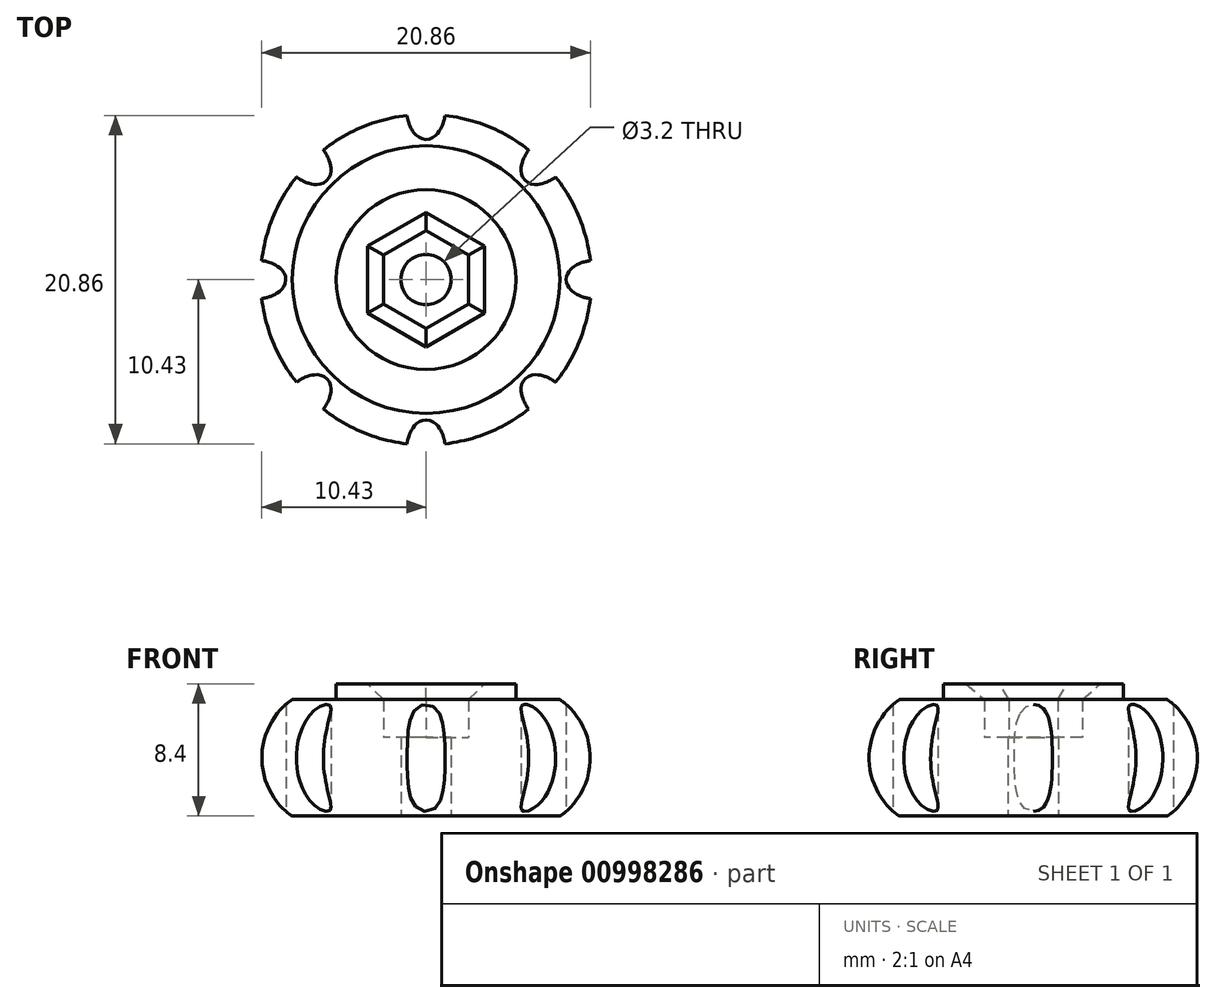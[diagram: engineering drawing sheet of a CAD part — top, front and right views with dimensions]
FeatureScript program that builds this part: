
annotation { "Feature Type Name" : "Feature", "Feature Type Description" : "" }
export const myFeature = defineFeature(function(context is Context, id is Id, definition is map)
    precondition{}
    {
        {
            var Q0;
            Q0=qCreatedBy(makeId("Top.planeOp"),FACE);
            var sketch = newSketch(context, id + "F0", { "sketchPlane" : qUnion([Q0])});
            skCircle(sketch, "E0", {"center": v(0, 0) * mm, "radius": 1.6 * mm});
            skCircle(sketch, "E1", {"center": v(0, 0) * mm, "radius": 8.5 * mm});
            skCircle(sketch, "E2.cCircle", {"center": v(0, 0) * mm, "radius": 2.7 * mm, "construction": true});
            skLineSegment(sketch, "E2.0", {"start": v(-2.7, 1.56) * mm, "end": v(0, 3.12) * mm});
            skLineSegment(sketch, "E2.1", {"start": v(0, 3.12) * mm, "end": v(2.7, 1.56) * mm});
            skLineSegment(sketch, "E2.2", {"start": v(2.7, 1.56) * mm, "end": v(2.7, -1.56) * mm});
            skLineSegment(sketch, "E2.3", {"start": v(2.7, -1.56) * mm, "end": v(0, -3.12) * mm});
            skLineSegment(sketch, "E2.4", {"start": v(0, -3.12) * mm, "end": v(-2.7, -1.56) * mm});
            skLineSegment(sketch, "E2.5", {"start": v(-2.7, -1.56) * mm, "end": v(-2.7, 1.56) * mm});
            skPoint(sketch, "E2.0.midPoint", {"position": v(-1.35, 2.34) * mm});
            skLineSegment(sketch, "E3", {"start": v(-8.5, 0) * mm, "end": v(8.5, 0) * mm, "construction": true});
            skSolve(sketch);
        }
        {
            var Q0;
            Q0=makeQuery(id+"F0.imprint","IMPRINT",FACE,{"disambiguationData":[TD([[makeQuery(id+"F0.imprint","IMPRINT",EDGE,{"derivedFrom":sQuery(id+"F0.wireOp",EDGE,"E1")}),1.0]])]});
            var Q1;
            Q1=makeQuery(id+"F0.imprint","IMPRINT",FACE,{"disambiguationData":[TD([[makeQuery(id+"F0.imprint","IMPRINT",EDGE,{"derivedFrom":sQuery(id+"F0.wireOp",EDGE,"E0")}),-1.0]])]});
            extrude(context, id + "F1", {"entities" : qUnion([Q0, Q1]), "depth" : 5 * mm, "offsetDistance" : 25 * mm});
        }
        {
            var Q0;
            Q0=makeQuery(id+"F0.imprint","IMPRINT",FACE,{"disambiguationData":[TD([[makeQuery(id+"F0.imprint","IMPRINT",EDGE,{"derivedFrom":sQuery(id+"F0.wireOp",EDGE,"E1")}),1.0]])]});
            extrude(context, id + "F2", {"entities" : qUnion([Q0]), "operationType" : NewBodyOperationType.ADD, "depth" : 7.4 * mm, "offsetDistance" : 25 * mm});
        }
        {
            var Q0;
            Q0=qCreatedBy(makeId("Front.planeOp"),FACE);
            var sketch = newSketch(context, id + "F3", { "sketchPlane" : qUnion([Q0])});
            skArc(sketch, "E4", {"start": v(8.5, 0) * mm, "mid": v(10.5, 3.7) * mm, "end": v(8.5, 7.4) * mm});
            skLineSegment(sketch, "E5", {"start": v(8.5, 7.4) * mm, "end": v(8.5, 0) * mm});
            skSolve(sketch);
        }
        {
            var Q0;
            Q0=makeQuery(id+"F3.imprint","IMPRINT",FACE,{"disambiguationData":[TD([[makeQuery(id+"F3.imprint","IMPRINT",EDGE,{"derivedFrom":sQuery(id+"F3.wireOp",EDGE,"E4")}),1.0]])]});
            var Q1;
            {var subQ0=sQuery(id+"F0.wireOp",EDGE,"E1");Q1=makeQuery(id+"F2.boolean.opBoolean","MERGE",FACE,{"derivedFrom":[makeQuery(id+"F1.opExtrude","SWEPT_FACE",FACE,{"disambiguationData":[OSD([subQ0])]}),makeQuery(id+"F2.opExtrude","SWEPT_FACE",FACE,{"disambiguationData":[OSD([subQ0])]})]});}
            revolve(context, id + "F4", {"operationType" : NewBodyOperationType.ADD, "surfaceOperationType" : NewSurfaceOperationType.NEW, "entities" : qUnion([Q0]), "axis" : qUnion([Q1]), "revolveType" : RevolveType.FULL});
        }
        {
            var Q0;
            Q0=qCreatedBy(makeId("Top.planeOp"),FACE);
            var sketch = newSketch(context, id + "F5", { "sketchPlane" : qUnion([Q0])});
            skEllipse(sketch, "E6", {"center": v(10.87, 0) * mm, "majorRadius": 1.97 * mm, "minorRadius": 1.24 * mm, "majorAxis": v(1, 0)});
            skSolve(sketch);
        }
        {
            var Q0;
            Q0=makeQuery(id+"F5.imprint","IMPRINT",FACE,{"disambiguationData":[TD([[makeQuery(id+"F5.imprint","IMPRINT",EDGE,{"derivedFrom":sQuery(id+"F5.wireOp",EDGE,"E6")}),1.0]])]});
            extrude(context, id + "F6", {"entities" : qUnion([Q0]), "depth" : 10 * mm, "offsetDistance" : 25 * mm});
        }
        {
            var Q0;
            Q0=makeQuery(id+"F6.opExtrude","SWEPT_BODY",BODY,{"disambiguationData":[OSD([sQuery(id+"F5.wireOp",EDGE,"E6")])]});
            var Q1;
            Q1=makeQuery(id+"F4.opRevolve","SWEPT_FACE",FACE,{"disambiguationData":[OSD([sQuery(id+"F3.wireOp",EDGE,"E4")])]});
            circularPattern(context, id + "F7", {"operationType" : NewBodyOperationType.REMOVE, "entities" : qUnion([Q0]), "axis" : qUnion([Q1]), "angle" : 360 * degree, "instanceCount" : 8, "equalSpace" : true});
        }
        {
            var Q0;
            Q0=makeQuery(id+"F2.opExtrude","CAP_FACE",FACE,{"disambiguationData":[OSD([sQuery(id+"F0.wireOp",EDGE,"E1"),sQuery(id+"F0.wireOp",EDGE,"E2.0"),sQuery(id+"F0.wireOp",EDGE,"E2.1"),sQuery(id+"F0.wireOp",EDGE,"E2.2"),sQuery(id+"F0.wireOp",EDGE,"E2.3"),sQuery(id+"F0.wireOp",EDGE,"E2.4"),sQuery(id+"F0.wireOp",EDGE,"E2.5")])],"isStart":false});
            var sketch = newSketch(context, id + "F8", { "sketchPlane" : qUnion([Q0])});
            skCircle(sketch, "E7", {"center": v(0, 0) * mm, "radius": 5.71 * mm});
            skSolve(sketch);
        }
        {
            var Q0;
            Q0=makeQuery(id+"F8.imprint","IMPRINT",FACE,{"disambiguationData":[TD([[makeQuery(id+"F8.imprint","IMPRINT",EDGE,{"derivedFrom":sQuery(id+"F8.wireOp",EDGE,"E7")}),1.0]])]});
            extrude(context, id + "F9", {"entities" : qUnion([Q0]), "operationType" : NewBodyOperationType.ADD, "depth" : 1 * mm, "offsetDistance" : 25 * mm});
        }
        {
            var Q0;
            Q0=makeQuery(id+"F9.opExtrude","CAP_EDGE",EDGE,{"disambiguationData":[OSD([sQuery(id+"F8.wireOp",EDGE,"E7")])],"isStart":false});
            var Q1;
            {var subQ0=sQuery(id+"F3.wireOp",EDGE,"E5");var subQ1=sQuery(id+"F3.wireOp",EDGE,"E4");Q1=makeQuery(id+"F4.boolean.opBoolean","MERGE",EDGE,{"derivedFrom":[makeQuery(id+"F2.opExtrude","CAP_EDGE",EDGE,{"disambiguationData":[OSD([sQuery(id+"F0.wireOp",EDGE,"E1")])],"isStart":false}),makeQuery(id+"F4.opRevolve","SWEPT_EDGE",EDGE,{"disambiguationData":[OSD([subQ1,subQ0]),TDD([makeQuery(id+"F3.imprint","INTERSECT",VERTEX,{"disambiguationData":[OD(1.0)],"derivedFrom":[subQ1,subQ0]})])]})]});}
            loft(context, id + "F10", {"bodyType" : ToolBodyType.SURFACE, "wireProfilesArray" : [{ "wireProfileEntities" : qUnion([Q0]) }, { "wireProfileEntities" : qUnion([Q1]) }]});
        }
        {
            var Q0;
            Q0=makeQuery(id+"F9.opExtrude","CAP_EDGE",EDGE,{"disambiguationData":[OSD([sQuery(id+"F0.wireOp",EDGE,"E2.3")])],"isStart":false});
            var Q1;
            Q1=makeQuery(id+"F9.opExtrude","CAP_EDGE",EDGE,{"disambiguationData":[OSD([sQuery(id+"F0.wireOp",EDGE,"E2.4")])],"isStart":false});
            var Q2;
            Q2=makeQuery(id+"F9.opExtrude","CAP_EDGE",EDGE,{"disambiguationData":[OSD([sQuery(id+"F0.wireOp",EDGE,"E2.5")])],"isStart":false});
            var Q3;
            Q3=makeQuery(id+"F9.opExtrude","CAP_EDGE",EDGE,{"disambiguationData":[OSD([sQuery(id+"F0.wireOp",EDGE,"E2.0")])],"isStart":false});
            var Q4;
            Q4=makeQuery(id+"F9.opExtrude","CAP_EDGE",EDGE,{"disambiguationData":[OSD([sQuery(id+"F0.wireOp",EDGE,"E2.1")])],"isStart":false});
            var Q5;
            Q5=makeQuery(id+"F9.opExtrude","CAP_EDGE",EDGE,{"disambiguationData":[OSD([sQuery(id+"F0.wireOp",EDGE,"E2.2")])],"isStart":false});
            chamfer(context, id + "F11", {"entities" : qUnion([Q0, Q1, Q2, Q3, Q4, Q5]), "width" : 1 * mm, "tangentPropagation" : true});
        }
    });
